# Revit family: Accessory-Towel_Bar-KOHLER-LOURE-K-11577T_1
name_source: partatom
category: Specialty Equipment
units: mm (PartAtom-declared; Revit-internal decimal feet)

## family parameters
Cut with Voids When Loaded = No
Host = Face
OmniClass Number = 23.31.25.25
OmniClass Title = Towel Bars
Part Type = Normal
Room Calculation Point = No
Round Connector Dimension = Use Diameter
Shared = No

## types (2) — shared parameters
ADA Compliant = No
Assembly Code = C1030200
Date Modified = 08/02/2022
Default Elevation = 42"
Description = HOTELIER/TOWEL SHELF
Height = 3 3/4"
Length = 24 13/16"
Manufacturer = Kohler Co.
Master Format 2014 = 10 28 00
Master Format 2014 Name = Toilet, Bath, and Laundry Accessories
Material = Premium Metal Construction
Product Documentation Link = https://files.kohler.com.cn
Product Name = LOURE
Product Page URL = https://www.kohler.com.cn
URL = http://www.kohler.com.cn
http://www.kohler.com.cn
http://www.kohler.com.cn
http://www.kohler.com.cn
http://www.kohler.com.cn
WaterSense Certified = No
Width = 11"

## per-type parameters (varying)
| type | Finish | Model | Type |
| CP-Polished Chrome | Kohler-Metal-CP-Polished_Chrome | K-11577T-CP | 1 |
| BV-Brushed Bronze | Kohler-Metal-BV-Brushed_Bronze | K-11577T-BV | 2 |

## geometry (parser evidence)
native form markers: Sweep x5
no freeform markers — native parametric forms only
